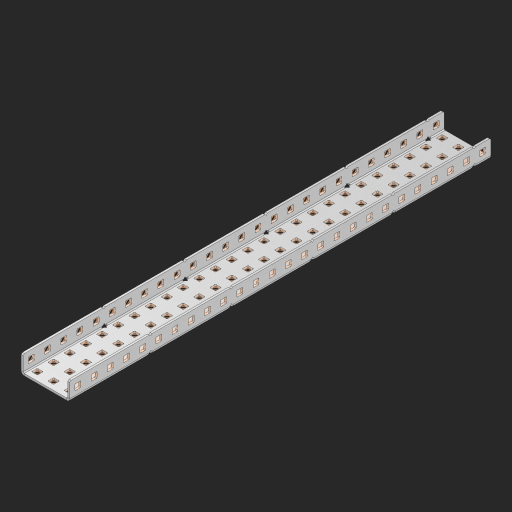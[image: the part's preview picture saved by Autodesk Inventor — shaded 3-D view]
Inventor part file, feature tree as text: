
AUTODESK INVENTOR PART (.ipt)
format: ipt  version: 2023 (Build 270158000, 158)  size: 1,654,272 bytes
history: native  units: in
note: dims shown in document units (in); Inventor stores cm internally (conversion verified against a paired STEP export)
features: other x135, extrude x129, sheet_metal_op x10, sketch x8, mirror x1, pattern_linear x1, chamfer x1
ambient origin geometry x8: Origin, YZ Plane, XZ Plane, XY Plane, X Axis, Y Axis, Z Axis, Center Point
bodies: Solid1 (feature_tree), Body (feature_tree)
feature tree (285):
  other  "Flange Pattern Plane"
  sheet_metal_op  "Flange Pattern"
  sheet_metal_op  "Body Pattern"
  other  "Arc Length"
  mirror  "Notch Mirror"
  pattern_linear  "Notch Pattern"  Spacing1=0.25in  [1 undecoded]
  chamfer  "End Chamfer"
  extrude  "Half Cut"  Depth=0.0625in
  sketch  "Sketch1"  dims[d0=1.5in]
  other  "Plate1"
  sketch  "Sketch2"  dims[d1=13.0in]
  other  "Plate2"
  sheet_metal_op  "Bend1"
  sheet_metal_op  "Corner1"
  sketch  "Sketch3"  dims[d2=0.0625in]
  other  "Flange Pattern Sketch"
  sketch  "Sketch7"  dims[d3=0.0625in]
  other  "Srf1"
  other  "Srf2"
  sketch  "Sketch8"  dims[d4=0.0312in]
  sketch  "Sketch9"  dims[d5=0.125in]
  other  "Srf91"
  sheet_metal_op  "Body Pattern Sketch"
  other  "Srf92"
  sketch  "Sketch13"  dims[d6=0.0625in]
  sketch  "Sketch14"  dims[d7=0.5in d8=90.0deg d9=0.0312in d10=0.25in d11=0.0625in d12=0.0625in d16=0.182in d17=0.02in d18=0.0625in d19=0.0in d20=0.25in d21=0.25in d46=0.172in d47=1.0in d48=0.0in d49=0.182in d50=0.02in d51=0.25in d52=0.25in d53=0.0625in d54=0.0in d55=0.172in d56=1.0in d57=0.0in d60=10.2362in d62=0.5in d63=1.1811in d65=0.5in d85=0.1473in d86=0.1782in d88=0.04in d89=0.0625in d90=0.0in d91=0.04in d92=0.0491in d95=2.5in d96=0.04in d97=0.25in d98=45.0deg d101=0.0in d102=2.497in d131=1.5in d132=10.2362in d134=0.5in d139=0.5in]
  other  "Srf856"
  other  "Srf1310"
  other  "Srf1311"
  other  "Srf1312"
  other  "Srf1376"
  other  "Srf1377"
  other  "Srf1728"
  other  "Srf1755"
  other  "Srf1878"
  other  "Srf1879"
  other  "Srf1880"
  other  "Srf1881"
  other  "Srf1882"
  other  "Srf1883"
  other  "Srf1884"
  other  "Srf1885"
  other  "Srf1886"
  other  "Srf1887"
  other  "Srf1888"
  other  "Srf1889"
  other  "Srf1890"
  other  "Srf1891"
  other  "Srf1892"
  other  "Srf1893"
  other  "Srf1894"
  other  "Srf1895"
  other  "Srf1896"
  other  "Srf1897"
  other  "Srf1898"
  other  "Srf1899"
  other  "Srf1900"
  other  "Srf1901"
  other  "Srf1902"
  other  "Srf1903"
  other  "Srf1904"
  other  "Srf1905"
  other  "Srf1906"
  other  "Srf1907"
  other  "Srf1908"
  other  "Srf1909"
  other  "Srf1910"
  other  "Srf1911"
  other  "Srf1912"
  other  "Srf1913"
  other  "Srf1914"
  other  "Srf1915"
  other  "Srf1916"
  other  "Srf1917"
  other  "Srf1918"
  other  "Srf1919"
  other  "Srf1920"
  other  "Srf1921"
  other  "Srf1922"
  other  "Srf1923"
  other  "Srf1942"
  other  "Srf1943"
  other  "Srf1944"
  other  "Srf1945"
  other  "Srf1946"
  other  "Srf1947"
  other  "Srf1948"
  other  "Srf1949"
  other  "Srf1950"
  other  "Srf1951"
  other  "Srf1952"
  other  "Srf1953"
  other  "Srf1954"
  other  "Srf1955"
  other  "Srf1956"
  other  "Srf1957"
  other  "Srf1958"
  other  "Srf1959"
  other  "Srf1960"
  other  "Srf1961"
  other  "Srf1962"
  other  "Srf1963"
  other  "Srf1964"
  other  "Srf1965"
  other  "Srf1966"
  other  "Srf1967"
  other  "Srf1968"
  other  "Srf1969"
  other  "Srf1970"
  other  "Srf1971"
  other  "Srf1972"
  other  "Srf1973"
  other  "Srf1974"
  other  "Srf1975"
  other  "Srf1976"
  other  "Srf1977"
  other  "Srf1978"
  other  "Srf1979"
  other  "Srf1980"
  other  "Srf1981"
  other  "Srf1982"
  other  "Srf1983"
  other  "Srf1984"
  other  "Srf1985"
  other  "Srf1986"
  other  "Srf1987"
  other  "Srf1988"
  other  "Srf1989"
  other  "Srf1990"
  other  "Srf1991"
  other  "Srf1992"
  other  "Srf1993"
  other  "Srf1994"
  other  "Srf1995"
  other  "Srf1996"
  other  "Srf1997"
  other  "Srf1998"
  other  "Srf1999"
  other  "Srf2000"
  other  "Srf2001"
  other  "Srf2002"
  other  "Srf2003"
  other  "Srf2004"
  other  "Srf2005"
  other  "Srf2006"
  other  "Srf2007"
  other  "Srf2008"
  other  "Srf2009"
  other  "Srf2010"
  other  "Srf2011"
  other  "Srf2012"
  other  "Srf2013"
  sheet_metal_op  "Flange Stamp"
  sheet_metal_op  "Flange Circle"
  sheet_metal_op  "Body Stamp"
  sheet_metal_op  "Body Circle"
  sheet_metal_op  "Notch"
  extrude  "ExtrusionSrf2"  Depth=0.0625in
  extrude  "ExtrusionSrf92"  Depth=1.5in
  extrude  "ExtrusionSrf856"  Depth=0.02in
  extrude  "ExtrusionSrf1310"  Depth=0.0625in
  extrude  "ExtrusionSrf1311"  TaperAngle=0.0deg  [1 undecoded]
  extrude  "ExtrusionSrf1312"  Depth=0.25in
  extrude  "ExtrusionSrf1376"  Depth=0.25in
  extrude  "ExtrusionSrf1377"  Depth=1.5in
  extrude  "ExtrusionSrf1728"  Depth=1.5in TaperAngle=0.0deg
  extrude  "ExtrusionSrf1755"  Depth=1.5in
  extrude  "ExtrusionSrf1878"  Depth=0.02in
  extrude  "ExtrusionSrf1879"  Depth=0.25in
  extrude  "ExtrusionSrf1880"  Depth=0.25in
  extrude  "ExtrusionSrf1881"  Depth=0.0625in
  extrude  "ExtrusionSrf1882"  TaperAngle=0.0deg  [1 undecoded]
  extrude  "ExtrusionSrf1883"  Depth=1.5in
  extrude  "ExtrusionSrf1884"  Depth=1.5in TaperAngle=0.0deg
  extrude  "ExtrusionSrf1885"  Depth=1.5in
  extrude  "ExtrusionSrf1886"  Depth=1.5in
  extrude  "ExtrusionSrf1887"  Depth=1.5in
  extrude  "ExtrusionSrf1888"  Depth=1.5in
  extrude  "ExtrusionSrf1889"  Depth=1.5in
  extrude  "ExtrusionSrf1890"  Depth=0.0625in
  extrude  "ExtrusionSrf1891"  TaperAngle=0.0deg  [1 undecoded]
  extrude  "ExtrusionSrf1892"  Depth=1.5in
  extrude  "ExtrusionSrf1893"  Depth=1.5in
  extrude  "ExtrusionSrf1894"  Depth=1.5in
  extrude  "ExtrusionSrf1895"  Depth=0.25in TaperAngle=45.0deg
  extrude  "ExtrusionSrf1896"  TaperAngle=0.0deg  [1 undecoded]
  extrude  "ExtrusionSrf1897"  Depth=1.5in
  extrude  "ExtrusionSrf1898"  Depth=1.5in
  extrude  "ExtrusionSrf1899"  Depth=1.5in
  extrude  "ExtrusionSrf1900"  Depth=1.5in
  extrude  "ExtrusionSrf1901"  Depth=1.5in
  extrude  "ExtrusionSrf1902"  [1 undecoded]
  extrude  "ExtrusionSrf1903"  [1 undecoded]
  extrude  "ExtrusionSrf1904"  [1 undecoded]
  extrude  "ExtrusionSrf1905"  [1 undecoded]
  extrude  "ExtrusionSrf1906"  [1 undecoded]
  extrude  "ExtrusionSrf1907"  [1 undecoded]
  extrude  "ExtrusionSrf1908"  [1 undecoded]
  extrude  "ExtrusionSrf1909"  [1 undecoded]
  extrude  "ExtrusionSrf1910"  [1 undecoded]
  extrude  "ExtrusionSrf1911"  [1 undecoded]
  extrude  "ExtrusionSrf1912"  [1 undecoded]
  extrude  "ExtrusionSrf1913"  [1 undecoded]
  extrude  "ExtrusionSrf1914"  [1 undecoded]
  extrude  "ExtrusionSrf1915"  [1 undecoded]
  extrude  "ExtrusionSrf1916"  [1 undecoded]
  extrude  "ExtrusionSrf1917"  [1 undecoded]
  extrude  "ExtrusionSrf1918"  [1 undecoded]
  extrude  "ExtrusionSrf1919"  [1 undecoded]
  extrude  "ExtrusionSrf1920"  [1 undecoded]
  extrude  "ExtrusionSrf1921"  [1 undecoded]
  extrude  "ExtrusionSrf1922"  [1 undecoded]
  extrude  "ExtrusionSrf1923"  [1 undecoded]
  extrude  "ExtrusionSrf1942"  [1 undecoded]
  extrude  "ExtrusionSrf1943"  [1 undecoded]
  extrude  "ExtrusionSrf1944"  [1 undecoded]
  extrude  "ExtrusionSrf1945"  [1 undecoded]
  extrude  "ExtrusionSrf1946"  [1 undecoded]
  extrude  "ExtrusionSrf1947"  [1 undecoded]
  extrude  "ExtrusionSrf1948"  [1 undecoded]
  extrude  "ExtrusionSrf1949"  [1 undecoded]
  extrude  "ExtrusionSrf1950"  [1 undecoded]
  extrude  "ExtrusionSrf1951"  [1 undecoded]
  extrude  "ExtrusionSrf1952"  [1 undecoded]
  extrude  "ExtrusionSrf1953"  [1 undecoded]
  extrude  "ExtrusionSrf1954"  [1 undecoded]
  extrude  "ExtrusionSrf1955"  [1 undecoded]
  extrude  "ExtrusionSrf1956"  [1 undecoded]
  extrude  "ExtrusionSrf1957"  [1 undecoded]
  extrude  "ExtrusionSrf1958"  [1 undecoded]
  extrude  "ExtrusionSrf1959"  [1 undecoded]
  extrude  "ExtrusionSrf1960"  [1 undecoded]
  extrude  "ExtrusionSrf1961"  [1 undecoded]
  extrude  "ExtrusionSrf1962"  [1 undecoded]
  extrude  "ExtrusionSrf1963"  [1 undecoded]
  extrude  "ExtrusionSrf1964"  [1 undecoded]
  extrude  "ExtrusionSrf1965"  [1 undecoded]
  extrude  "ExtrusionSrf1966"  [1 undecoded]
  extrude  "ExtrusionSrf1967"  [1 undecoded]
  extrude  "ExtrusionSrf1968"  [1 undecoded]
  extrude  "ExtrusionSrf1969"  [1 undecoded]
  extrude  "ExtrusionSrf1970"  [1 undecoded]
  extrude  "ExtrusionSrf1971"  [1 undecoded]
  extrude  "ExtrusionSrf1972"  [1 undecoded]
  extrude  "ExtrusionSrf1973"  [1 undecoded]
  extrude  "ExtrusionSrf1974"  [1 undecoded]
  extrude  "ExtrusionSrf1975"  [1 undecoded]
  extrude  "ExtrusionSrf1976"  [1 undecoded]
  extrude  "ExtrusionSrf1977"  [1 undecoded]
  extrude  "ExtrusionSrf1978"  [1 undecoded]
  extrude  "ExtrusionSrf1979"  [1 undecoded]
  extrude  "ExtrusionSrf1980"  [1 undecoded]
  extrude  "ExtrusionSrf1981"  [1 undecoded]
  extrude  "ExtrusionSrf1982"  [1 undecoded]
  extrude  "ExtrusionSrf1983"  [1 undecoded]
  extrude  "ExtrusionSrf1984"  [1 undecoded]
  extrude  "ExtrusionSrf1985"  [1 undecoded]
  extrude  "ExtrusionSrf1986"  [1 undecoded]
  extrude  "ExtrusionSrf1987"  [1 undecoded]
  extrude  "ExtrusionSrf1988"  [1 undecoded]
  extrude  "ExtrusionSrf1989"  [1 undecoded]
  extrude  "ExtrusionSrf1990"  [1 undecoded]
  extrude  "ExtrusionSrf1991"  [1 undecoded]
  extrude  "ExtrusionSrf1992"  [1 undecoded]
  extrude  "ExtrusionSrf1993"  [1 undecoded]
  extrude  "ExtrusionSrf1994"  [1 undecoded]
  extrude  "ExtrusionSrf1995"  [1 undecoded]
  extrude  "ExtrusionSrf1996"  [1 undecoded]
  extrude  "ExtrusionSrf1997"  [1 undecoded]
  extrude  "ExtrusionSrf1998"  [1 undecoded]
  extrude  "ExtrusionSrf1999"  [1 undecoded]
  extrude  "ExtrusionSrf2000"  [1 undecoded]
  extrude  "ExtrusionSrf2001"  [1 undecoded]
  extrude  "ExtrusionSrf2002"  [1 undecoded]
  extrude  "ExtrusionSrf2003"  [1 undecoded]
  extrude  "ExtrusionSrf2004"  [1 undecoded]
  extrude  "ExtrusionSrf2005"  [1 undecoded]
  extrude  "ExtrusionSrf2006"  [1 undecoded]
  extrude  "ExtrusionSrf2007"  [1 undecoded]
  extrude  "ExtrusionSrf2008"  [1 undecoded]
  extrude  "ExtrusionSrf2009"  [1 undecoded]
  extrude  "ExtrusionSrf2010"  [1 undecoded]
  extrude  "ExtrusionSrf2011"  [1 undecoded]
  extrude  "ExtrusionSrf2012"  [1 undecoded]
  extrude  "ExtrusionSrf2013"  [1 undecoded]
note: 99 required parameter values undecoded (feature->parameter linkage not recoverable at this tier; creation-order binding heuristic only, values carry confidence <= 0.55)
